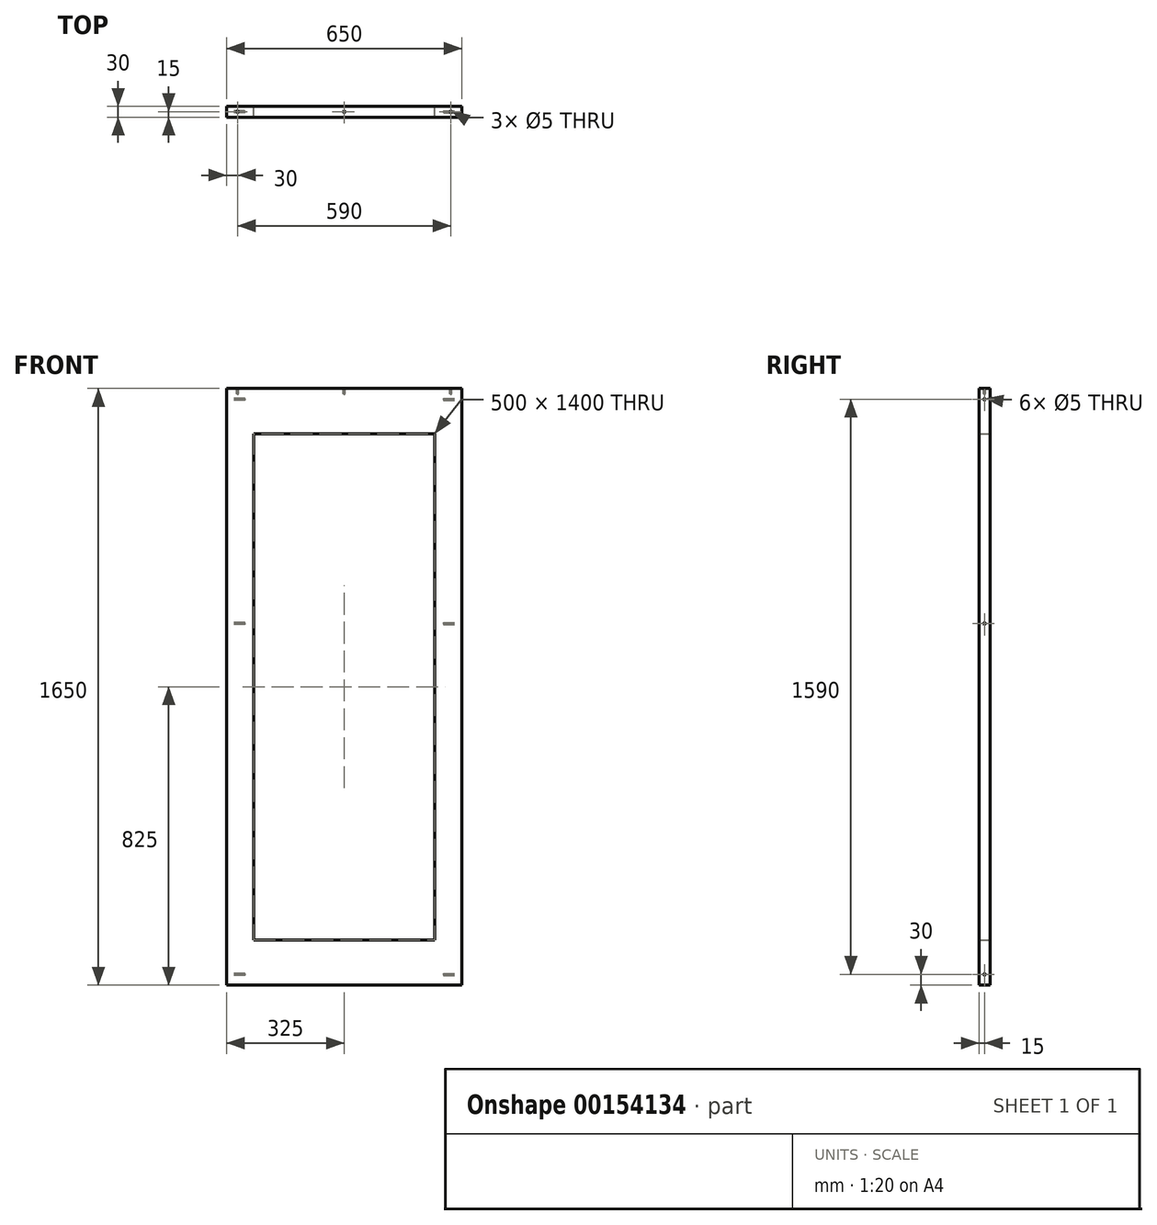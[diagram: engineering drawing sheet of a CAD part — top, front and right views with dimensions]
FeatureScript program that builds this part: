
annotation { "Feature Type Name" : "Feature", "Feature Type Description" : "" }
export const myFeature = defineFeature(function(context is Context, id is Id, definition is map)
    precondition{}
    {
        {
            var Q0;
            Q0=qCreatedBy(makeId("Front.planeOp"),FACE);
            var sketch = newSketch(context, id + "F0", { "sketchPlane" : qUnion([Q0])});
            skLineSegment(sketch, "E0.bottom", {"start": v(-325, -825) * mm, "end": v(325, -825) * mm});
            skLineSegment(sketch, "E0.top", {"start": v(-325, 825) * mm, "end": v(325, 825) * mm});
            skLineSegment(sketch, "E0.left", {"start": v(-325, -825) * mm, "end": v(-325, 825) * mm});
            skLineSegment(sketch, "E0.right", {"start": v(325, -825) * mm, "end": v(325, 825) * mm});
            skPoint(sketch, "E0.middle", {"position": v(0, 0) * mm});
            skLineSegment(sketch, "E1.bottom", {"start": v(-250, -700) * mm, "end": v(250, -700) * mm});
            skLineSegment(sketch, "E1.top", {"start": v(-250, 700) * mm, "end": v(250, 700) * mm});
            skLineSegment(sketch, "E1.left", {"start": v(-250, -700) * mm, "end": v(-250, 700) * mm});
            skLineSegment(sketch, "E1.right", {"start": v(250, -700) * mm, "end": v(250, 700) * mm});
            skSolve(sketch);
        }
        {
            var Q0;
            Q0=makeQuery(id+"F0.imprint","IMPRINT",FACE,{"disambiguationData":[TD([[makeQuery(id+"F0.imprint","IMPRINT",EDGE,{"derivedFrom":sQuery(id+"F0.wireOp",EDGE,"E0.bottom")}),1.0]])]});
            extrude(context, id + "F1", {"entities" : qUnion([Q0]), "depth" : 30 * mm});
        }
        {
            var Q0;
            Q0=makeQuery(id+"F1.opExtrude","SWEPT_FACE",FACE,{"disambiguationData":[OSD([sQuery(id+"F0.wireOp",EDGE,"E0.left")])]});
            cPlane(context, id + "F2", {"entities" : qUnion([Q0]), "cplaneType" : CPlaneType.OFFSET, "offset" : 0 * mm, "width" : 150 * mm, "height" : 150 * mm});
        }
        {
            var Q0;
            Q0=makeQuery(id+"F1.opExtrude","SWEPT_FACE",FACE,{"disambiguationData":[OSD([sQuery(id+"F0.wireOp",EDGE,"E0.right")])]});
            cPlane(context, id + "F3", {"entities" : qUnion([Q0]), "cplaneType" : CPlaneType.OFFSET, "offset" : 0 * mm, "width" : 150 * mm, "height" : 150 * mm});
        }
        {
            var Q0;
            Q0=qCreatedBy(id+"F2.planeOp",FACE);
            var sketch = newSketch(context, id + "F4", { "sketchPlane" : qUnion([Q0])});
            skLineSegment(sketch, "E2", {"start": v(30, 825) * mm, "end": v(0, 825) * mm});
            skLineSegment(sketch, "E3", {"start": v(30, 825) * mm, "end": v(30, -825) * mm});
            skLineSegment(sketch, "E4", {"start": v(0, -825) * mm, "end": v(30, -825) * mm});
            skLineSegment(sketch, "E5", {"start": v(0, -825) * mm, "end": v(0, 825) * mm});
            skPoint(sketch, "E6", {"position": v(15, 795) * mm});
            skPoint(sketch, "E7", {"position": v(15, 175) * mm});
            skPoint(sketch, "E8", {"position": v(15, -795) * mm});
            skSolve(sketch);
        }
        {
            var Q0;
            Q0=sQuery(id+"F4.wireOp",VERTEX,"E6");
            var Q1;
            Q1=sQuery(id+"F4.wireOp",VERTEX,"E7");
            var Q2;
            Q2=sQuery(id+"F4.wireOp",VERTEX,"E8");
            var Q3;
            Q3=makeQuery(id+"F1.opExtrude","SWEPT_BODY",BODY,{"disambiguationData":[OSD([sQuery(id+"F0.wireOp",EDGE,"E0.bottom"),sQuery(id+"F0.wireOp",EDGE,"E0.top"),sQuery(id+"F0.wireOp",EDGE,"E0.left"),sQuery(id+"F0.wireOp",EDGE,"E0.right"),sQuery(id+"F0.wireOp",EDGE,"E1.bottom"),sQuery(id+"F0.wireOp",EDGE,"E1.top"),sQuery(id+"F0.wireOp",EDGE,"E1.left"),sQuery(id+"F0.wireOp",EDGE,"E1.right")])]});
            hole(context, id + "F5", {"style" : HoleStyle.SIMPLE, "endStyle" : HoleEndStyle.BLIND, "standardTappedOrClearance" : lookupTablePath({ "standard" : "ISO", "engagement" : "75%", "pitch" : "1 mm", "size" : "M6", "type" : "Tapped" }), "standardBlindInLast" : lookupTablePath({ "standard" : "ISO", "engagement" : "75%", "pitch" : "1 mm", "size" : "M6", "type" : "Tapped" }), "holeDiameter" : 5 * mm, "holeDepth" : 50 * mm, "locations" : qUnion([Q0, Q1, Q2]), "scope" : qUnion([Q3]), "majorDiameter" : 6 * mm});
        }
        {
            var Q0;
            Q0=qCreatedBy(id+"F3.planeOp",FACE);
            var sketch = newSketch(context, id + "F6", { "sketchPlane" : qUnion([Q0])});
            skLineSegment(sketch, "E9", {"start": v(0, 825) * mm, "end": v(-30, 825) * mm});
            skLineSegment(sketch, "E10", {"start": v(0, 825) * mm, "end": v(0, -825) * mm});
            skLineSegment(sketch, "E11", {"start": v(-30, -825) * mm, "end": v(0, -825) * mm});
            skLineSegment(sketch, "E12", {"start": v(-30, -825) * mm, "end": v(-30, 825) * mm});
            skPoint(sketch, "E13", {"position": v(-15, 795) * mm});
            skPoint(sketch, "E14", {"position": v(-15, 175) * mm});
            skPoint(sketch, "E15", {"position": v(-15, -795) * mm});
            skSolve(sketch);
        }
        {
            var Q0;
            Q0=sQuery(id+"F6.wireOp",VERTEX,"E13");
            var Q1;
            Q1=sQuery(id+"F6.wireOp",VERTEX,"E14");
            var Q2;
            Q2=sQuery(id+"F6.wireOp",VERTEX,"E15");
            var Q3;
            Q3=makeQuery(id+"F1.opExtrude","SWEPT_BODY",BODY,{"disambiguationData":[OSD([sQuery(id+"F0.wireOp",EDGE,"E0.bottom"),sQuery(id+"F0.wireOp",EDGE,"E0.top"),sQuery(id+"F0.wireOp",EDGE,"E0.left"),sQuery(id+"F0.wireOp",EDGE,"E0.right"),sQuery(id+"F0.wireOp",EDGE,"E1.bottom"),sQuery(id+"F0.wireOp",EDGE,"E1.top"),sQuery(id+"F0.wireOp",EDGE,"E1.left"),sQuery(id+"F0.wireOp",EDGE,"E1.right")])]});
            hole(context, id + "F7", {"style" : HoleStyle.SIMPLE, "endStyle" : HoleEndStyle.BLIND, "standardTappedOrClearance" : lookupTablePath({ "standard" : "ISO", "engagement" : "75%", "pitch" : "1 mm", "size" : "M6", "type" : "Tapped" }), "standardBlindInLast" : lookupTablePath({ "standard" : "ISO", "engagement" : "75%", "pitch" : "1 mm", "size" : "M6", "type" : "Tapped" }), "holeDiameter" : 5 * mm, "holeDepth" : 50 * mm, "locations" : qUnion([Q0, Q1, Q2]), "scope" : qUnion([Q3]), "majorDiameter" : 6 * mm});
        }
        {
            var Q0;
            Q0=makeQuery(id+"F1.opExtrude","SWEPT_FACE",FACE,{"disambiguationData":[OSD([sQuery(id+"F0.wireOp",EDGE,"E0.top")])]});
            cPlane(context, id + "F8", {"entities" : qUnion([Q0]), "cplaneType" : CPlaneType.OFFSET, "offset" : 0 * mm, "width" : 150 * mm, "height" : 150 * mm});
        }
        {
            var Q0;
            Q0=qCreatedBy(id+"F8.planeOp",FACE);
            var sketch = newSketch(context, id + "F9", { "sketchPlane" : qUnion([Q0])});
            skLineSegment(sketch, "E16.bottom", {"start": v(-325, 0) * mm, "end": v(325, 0) * mm});
            skLineSegment(sketch, "E16.top", {"start": v(-325, -30) * mm, "end": v(325, -30) * mm});
            skLineSegment(sketch, "E16.left", {"start": v(-325, 0) * mm, "end": v(-325, -30) * mm});
            skLineSegment(sketch, "E16.right", {"start": v(325, 0) * mm, "end": v(325, -30) * mm});
            skPoint(sketch, "E17", {"position": v(-295, -15) * mm});
            skPoint(sketch, "E18", {"position": v(295, -15) * mm});
            skPoint(sketch, "E19", {"position": v(0, -15) * mm});
            skSolve(sketch);
        }
        {
            var Q0;
            Q0=sQuery(id+"F9.wireOp",VERTEX,"E17");
            var Q1;
            Q1=sQuery(id+"F9.wireOp",VERTEX,"E19");
            var Q2;
            Q2=sQuery(id+"F9.wireOp",VERTEX,"E18");
            var Q3;
            Q3=makeQuery(id+"F1.opExtrude","SWEPT_BODY",BODY,{"disambiguationData":[OSD([sQuery(id+"F0.wireOp",EDGE,"E0.bottom"),sQuery(id+"F0.wireOp",EDGE,"E0.top"),sQuery(id+"F0.wireOp",EDGE,"E0.left"),sQuery(id+"F0.wireOp",EDGE,"E0.right"),sQuery(id+"F0.wireOp",EDGE,"E1.bottom"),sQuery(id+"F0.wireOp",EDGE,"E1.top"),sQuery(id+"F0.wireOp",EDGE,"E1.left"),sQuery(id+"F0.wireOp",EDGE,"E1.right")])]});
            hole(context, id + "F10", {"style" : HoleStyle.SIMPLE, "endStyle" : HoleEndStyle.BLIND, "standardTappedOrClearance" : lookupTablePath({ "standard" : "ISO", "engagement" : "75%", "pitch" : "1 mm", "size" : "M6", "type" : "Tapped" }), "standardBlindInLast" : lookupTablePath({ "standard" : "ISO", "engagement" : "75%", "pitch" : "1 mm", "size" : "M6", "type" : "Tapped" }), "holeDiameter" : 5 * mm, "holeDepth" : 15 * mm, "locations" : qUnion([Q0, Q1, Q2]), "scope" : qUnion([Q3]), "majorDiameter" : 6 * mm});
        }
    });
